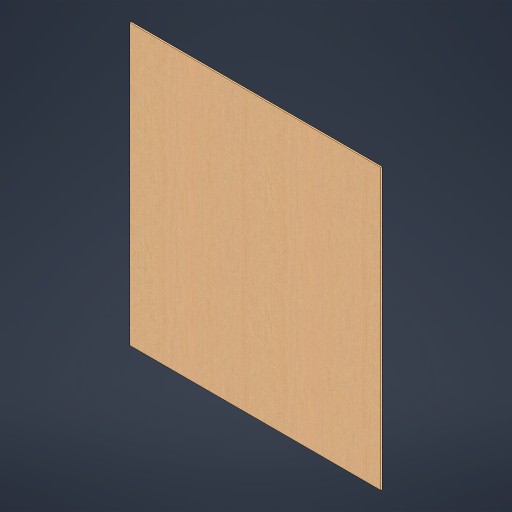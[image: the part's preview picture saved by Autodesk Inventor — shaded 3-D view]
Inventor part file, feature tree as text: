
AUTODESK INVENTOR PART (.ipt)
format: ipt  version: 2024 (Build 280153000, 153)  size: 312,320 bytes
history: native  units: mm
features: other x2, extrude x1, sketch x1
ambient origin geometry x8: Origin, YZ Plane, XZ Plane, XY Plane, X Axis, Y Axis, Z Axis, Center Point
bodies: Body1 (feature_tree)
feature tree (4):
  other  "솔리드1"
  extrude  "돌출1"  Depth=530.0mm
  sketch  "스케치1"
  other  "Finish1"
